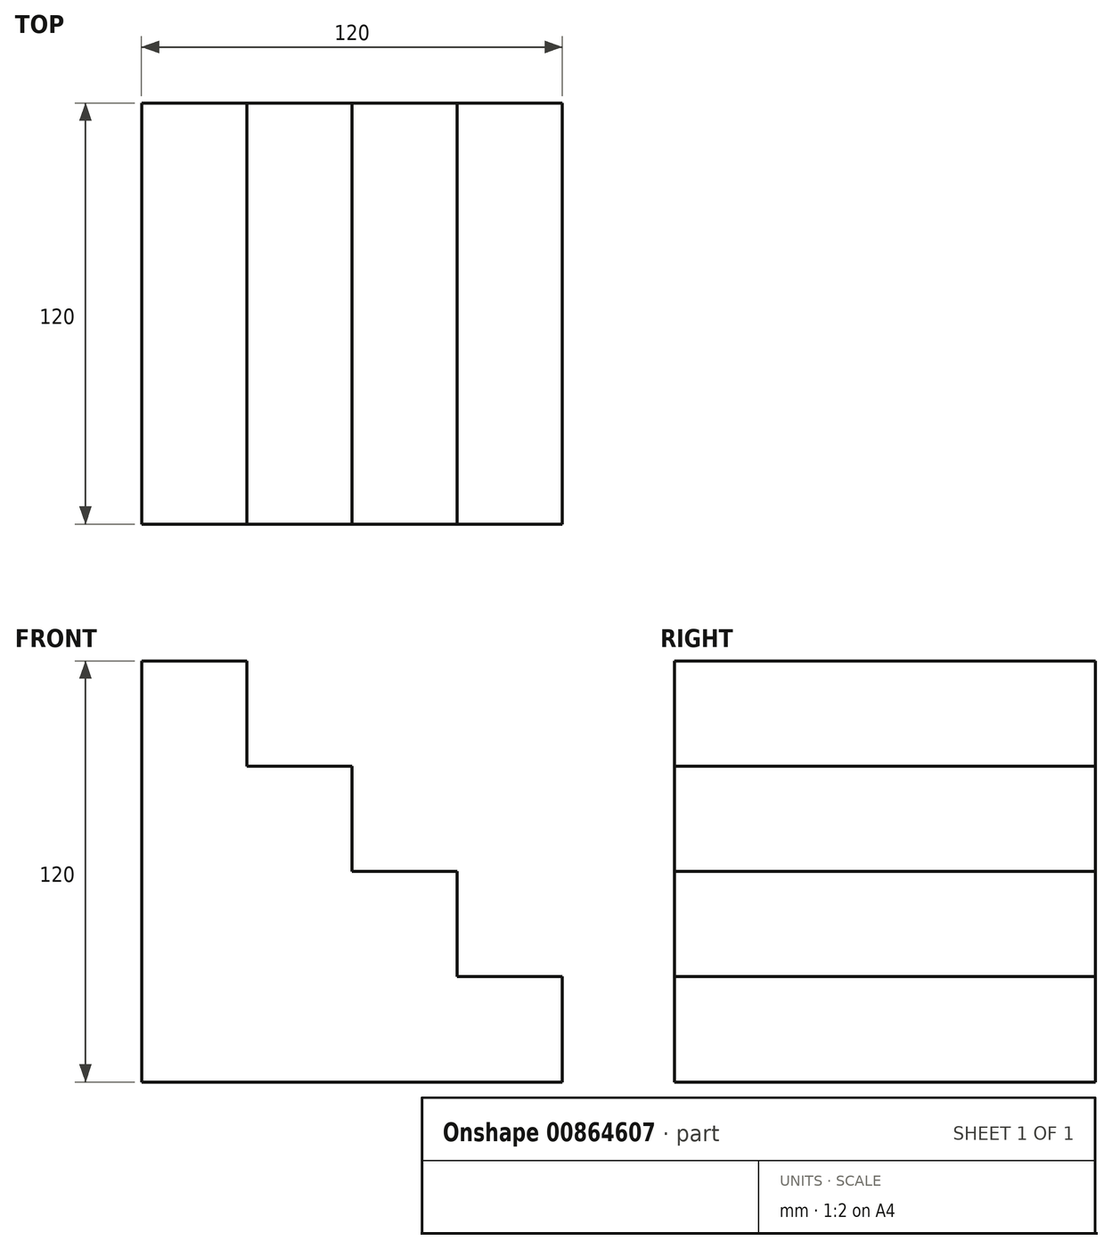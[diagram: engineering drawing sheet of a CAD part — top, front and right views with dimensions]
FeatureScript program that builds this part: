
annotation { "Feature Type Name" : "Feature", "Feature Type Description" : "" }
export const myFeature = defineFeature(function(context is Context, id is Id, definition is map)
    precondition{}
    {
        {
            var Q0;
            Q0=qCreatedBy(makeId("Front.planeOp"),FACE);
            var sketch = newSketch(context, id + "F0", { "sketchPlane" : qUnion([Q0])});
            skLineSegment(sketch, "E0.bottom", {"start": v(-69.37, -44.33) * mm, "end": v(50.63, -44.33) * mm});
            skLineSegment(sketch, "E0.top", {"start": v(-69.37, -74.33) * mm, "end": v(50.63, -74.33) * mm});
            skLineSegment(sketch, "E0.left", {"start": v(-69.37, -44.33) * mm, "end": v(-69.37, -74.33) * mm});
            skLineSegment(sketch, "E0.right", {"start": v(50.63, -44.33) * mm, "end": v(50.63, -74.33) * mm});
            skLineSegment(sketch, "E1.bottom", {"start": v(-69.37, -44.33) * mm, "end": v(20.63, -44.33) * mm});
            skLineSegment(sketch, "E1.top", {"start": v(-69.37, -14.33) * mm, "end": v(20.63, -14.33) * mm});
            skLineSegment(sketch, "E1.left", {"start": v(-69.37, -44.33) * mm, "end": v(-69.37, -14.33) * mm});
            skLineSegment(sketch, "E1.right", {"start": v(20.63, -44.33) * mm, "end": v(20.63, -14.33) * mm});
            skLineSegment(sketch, "E2.bottom", {"start": v(-69.37, -14.33) * mm, "end": v(-9.37, -14.33) * mm});
            skLineSegment(sketch, "E2.top", {"start": v(-69.37, 15.67) * mm, "end": v(-9.37, 15.67) * mm});
            skLineSegment(sketch, "E2.left", {"start": v(-69.37, -14.33) * mm, "end": v(-69.37, 15.67) * mm});
            skLineSegment(sketch, "E2.right", {"start": v(-9.37, -14.33) * mm, "end": v(-9.37, 15.67) * mm});
            skLineSegment(sketch, "E3.bottom", {"start": v(-69.37, 45.67) * mm, "end": v(-39.37, 45.67) * mm});
            skLineSegment(sketch, "E3.top", {"start": v(-69.37, 15.67) * mm, "end": v(-39.37, 15.67) * mm});
            skLineSegment(sketch, "E3.left", {"start": v(-69.37, 45.67) * mm, "end": v(-69.37, 15.67) * mm});
            skLineSegment(sketch, "E3.right", {"start": v(-39.37, 45.67) * mm, "end": v(-39.37, 15.67) * mm});
            skSolve(sketch);
        }
        {
            var Q0;
            Q0 = qSketchRegion(id + "F0", true);
            extrude(context, id + "F1", {"entities" : qUnion([Q0]), "endBound" : BoundingType.SYMMETRIC, "depth" : 120 * mm, "offsetDistance" : 25.4 * mm});
        }
    });
